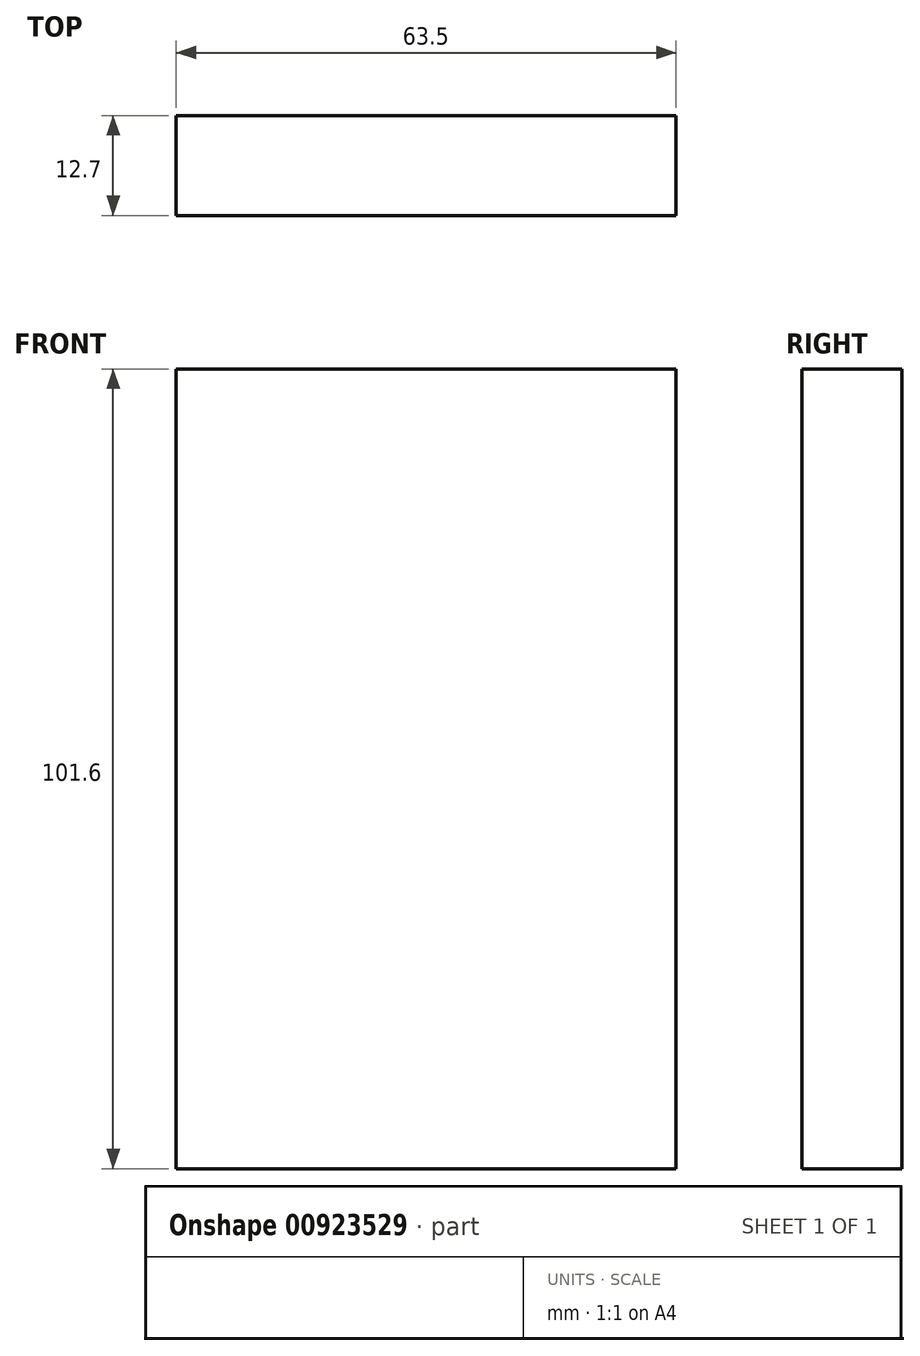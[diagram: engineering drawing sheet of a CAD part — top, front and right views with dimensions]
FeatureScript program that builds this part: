
annotation { "Feature Type Name" : "Feature", "Feature Type Description" : "" }
export const myFeature = defineFeature(function(context is Context, id is Id, definition is map)
    precondition{}
    {
        {
            var Q0;
            Q0=qCreatedBy(makeId("Front.planeOp"),FACE);
            var sketch = newSketch(context, id + "F0", { "sketchPlane" : qUnion([Q0])});
            skLineSegment(sketch, "E0.bottom", {"start": v(31.75, 50.8) * mm, "end": v(-31.75, 50.8) * mm});
            skLineSegment(sketch, "E0.top", {"start": v(31.75, -50.8) * mm, "end": v(-31.75, -50.8) * mm});
            skLineSegment(sketch, "E0.left", {"start": v(31.75, 50.8) * mm, "end": v(31.75, -50.8) * mm});
            skLineSegment(sketch, "E0.right", {"start": v(-31.75, 50.8) * mm, "end": v(-31.75, -50.8) * mm});
            skPoint(sketch, "E0.middle", {"position": v(0, 0) * mm});
            skSolve(sketch);
        }
        {
            var Q0;
            Q0=makeQuery(id+"F0.imprint","IMPRINT",FACE,{"disambiguationData":[TD([[makeQuery(id+"F0.imprint","IMPRINT",EDGE,{"derivedFrom":sQuery(id+"F0.wireOp",EDGE,"E0.bottom")}),1.0]])]});
            extrude(context, id + "F1", {"entities" : qUnion([Q0]), "depth" : 12.7 * mm, "offsetDistance" : 25.4 * mm});
        }
    });
